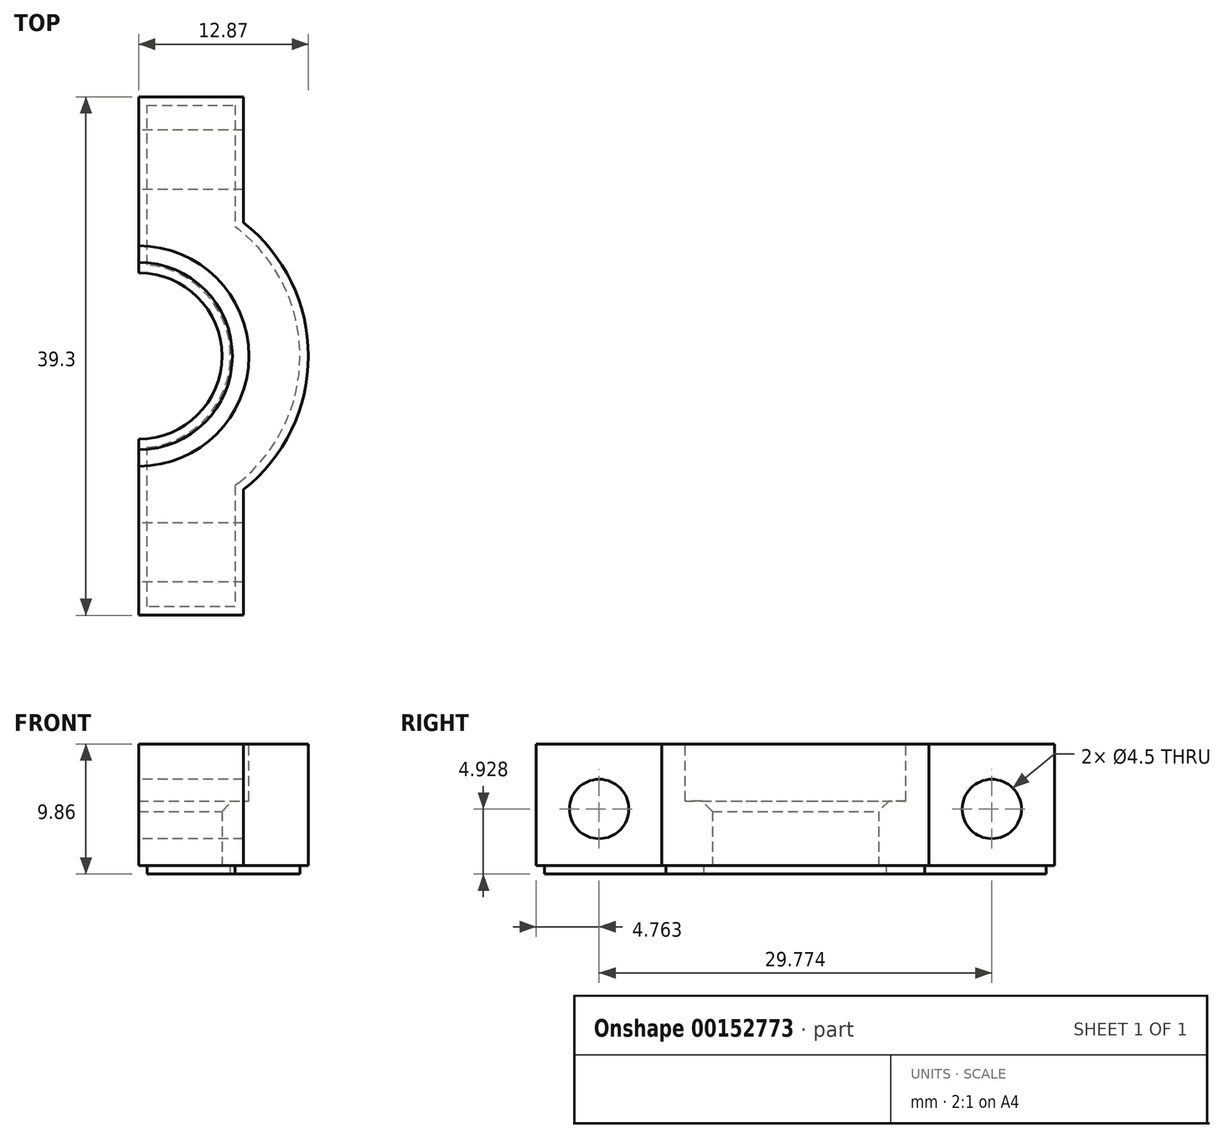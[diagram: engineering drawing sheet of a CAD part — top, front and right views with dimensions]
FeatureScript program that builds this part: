
annotation { "Feature Type Name" : "Feature", "Feature Type Description" : "" }
export const myFeature = defineFeature(function(context is Context, id is Id, definition is map)
    precondition{}
    {
        {
            var Q0;
            Q0=qCreatedBy(makeId("Top.planeOp"),FACE);
            var sketch = newSketch(context, id + "F0", { "sketchPlane" : qUnion([Q0])});
            skArc(sketch, "E0", {"start": v(7.94, -10.12) * mm, "mid": v(12.87, 0) * mm, "end": v(7.94, 10.12) * mm});
            skLineSegment(sketch, "E1", {"start": v(7.94, -10.12) * mm, "end": v(7.94, -19.65) * mm});
            skLineSegment(sketch, "E2", {"start": v(7.94, -19.65) * mm, "end": v(0, -19.65) * mm});
            skLineSegment(sketch, "E3", {"start": v(0, -19.65) * mm, "end": v(0, -6.31) * mm});
            skLineSegment(sketch, "E4", {"start": v(0, -6.31) * mm, "end": v(0, 6.31) * mm, "construction": true});
            skLineSegment(sketch, "E5", {"start": v(0, 6.31) * mm, "end": v(0, 19.65) * mm});
            skLineSegment(sketch, "E6", {"start": v(0, 19.65) * mm, "end": v(7.94, 19.65) * mm});
            skLineSegment(sketch, "E7", {"start": v(7.94, 19.65) * mm, "end": v(7.94, 10.12) * mm});
            skArc(sketch, "E8", {"start": v(0, -6.31) * mm, "mid": v(6.31, 0) * mm, "end": v(0, 6.31) * mm});
            skSolve(sketch);
        }
        {
            var Q0;
            Q0=makeQuery(id+"F0.imprint","IMPRINT",FACE,{"disambiguationData":[TD([[makeQuery(id+"F0.imprint","IMPRINT",EDGE,{"derivedFrom":sQuery(id+"F0.wireOp",EDGE,"1THsXMdy-5DrS-CnlL-Ftxn-9wsGK0M0J4RZ")}),-1.0]])]});
            var Q1;
            Q1=makeQuery(id+"F0.imprint","IMPRINT",FACE,{"disambiguationData":[TD([[makeQuery(id+"F0.imprint","IMPRINT",EDGE,{"derivedFrom":sQuery(id+"F0.wireOp",EDGE,"E0")}),1.0]])]});
            extrude(context, id + "F1", {"entities" : qUnion([Q0, Q1]), "depth" : 9.86 * mm});
        }
        {
            var Q0;
            Q0=makeQuery(id+"F1.opExtrude","SWEPT_FACE",FACE,{"disambiguationData":[OSD([sQuery(id+"F0.wireOp",EDGE,"E2")])]});
            var sketch = newSketch(context, id + "F2", { "sketchPlane" : qUnion([Q0])});
            skLineSegment(sketch, "E9.bottom", {"start": v(0.63, 0) * mm, "end": v(0, 0) * mm});
            skLineSegment(sketch, "E9.top", {"start": v(0.63, 0.63) * mm, "end": v(0, 0.63) * mm});
            skLineSegment(sketch, "E9.left", {"start": v(0.63, 0) * mm, "end": v(0.63, 0.63) * mm});
            skLineSegment(sketch, "E9.right", {"start": v(0, 0) * mm, "end": v(0, 0.63) * mm});
            skSolve(sketch);
        }
        {
            var Q0;
            Q0=makeQuery(id+"F2.imprint","IMPRINT",FACE,{"disambiguationData":[TD([[makeQuery(id+"F2.imprint","IMPRINT",EDGE,{"derivedFrom":sQuery(id+"F2.wireOp",EDGE,"E9.bottom")}),-1.0]])]});
            var Q1;
            Q1=makeQuery(id+"F1.opExtrude","CAP_EDGE",EDGE,{"disambiguationData":[OSD([sQuery(id+"F0.wireOp",EDGE,"E3")])],"isStart":true});
            var Q2;
            Q2=makeQuery(id+"F1.opExtrude","CAP_EDGE",EDGE,{"disambiguationData":[OSD([sQuery(id+"F0.wireOp",EDGE,"E8")])],"isStart":true});
            var Q3;
            Q3=makeQuery(id+"F1.opExtrude","CAP_EDGE",EDGE,{"disambiguationData":[OSD([sQuery(id+"F0.wireOp",EDGE,"E5")])],"isStart":true});
            var Q4;
            Q4=makeQuery(id+"F1.opExtrude","CAP_EDGE",EDGE,{"disambiguationData":[OSD([sQuery(id+"F0.wireOp",EDGE,"E6")])],"isStart":true});
            var Q5;
            Q5=makeQuery(id+"F1.opExtrude","CAP_EDGE",EDGE,{"disambiguationData":[OSD([sQuery(id+"F0.wireOp",EDGE,"E7")])],"isStart":true});
            var Q6;
            Q6=makeQuery(id+"F1.opExtrude","CAP_EDGE",EDGE,{"disambiguationData":[OSD([sQuery(id+"F0.wireOp",EDGE,"E0")])],"isStart":true});
            var Q7;
            Q7=makeQuery(id+"F1.opExtrude","CAP_EDGE",EDGE,{"disambiguationData":[OSD([sQuery(id+"F0.wireOp",EDGE,"E1")])],"isStart":true});
            var Q8;
            Q8=makeQuery(id+"F1.opExtrude","CAP_EDGE",EDGE,{"disambiguationData":[OSD([sQuery(id+"F0.wireOp",EDGE,"E2")])],"isStart":true});
            sweep(context, id + "F3", {"operationType" : NewBodyOperationType.REMOVE, "profiles" : qUnion([Q0]), "path" : qUnion([Q1, Q2, Q3, Q4, Q5, Q6, Q7, Q8])});
        }
        {
            var Q0;
            Q0=makeQuery(id+"F1.opExtrude","CAP_FACE",FACE,{"disambiguationData":[OSD([sQuery(id+"F0.wireOp",EDGE,"E0"),sQuery(id+"F0.wireOp",EDGE,"E1"),sQuery(id+"F0.wireOp",EDGE,"E2"),sQuery(id+"F0.wireOp",EDGE,"E3"),sQuery(id+"F0.wireOp",EDGE,"E5"),sQuery(id+"F0.wireOp",EDGE,"E6"),sQuery(id+"F0.wireOp",EDGE,"E7"),sQuery(id+"F0.wireOp",EDGE,"E8")])],"isStart":false});
            var sketch = newSketch(context, id + "F4", { "sketchPlane" : qUnion([Q0])});
            skLineSegment(sketch, "E10", {"start": v(0, 8.36) * mm, "end": v(0, -8.36) * mm});
            skArc(sketch, "E11", {"start": v(0, -8.36) * mm, "mid": v(8.36, 0) * mm, "end": v(0, 8.36) * mm});
            skSolve(sketch);
        }
        {
            var Q0;
            Q0 = qSketchRegion(id + "F4", true);
            extrude(context, id + "F5", {"entities" : qUnion([Q0]), "operationType" : NewBodyOperationType.REMOVE, "oppositeDirection" : true, "depth" : 4.32 * mm});
        }
        {
            var Q0;
            Q0=makeQuery(id+"F5.boolean.opBoolean","INTERSECT",EDGE,{"derivedFrom":[makeQuery(id+"F1.opExtrude","SWEPT_FACE",FACE,{"disambiguationData":[OSD([sQuery(id+"F0.wireOp",EDGE,"E8")])]}),makeQuery(id+"F5.opExtrude","CAP_FACE",FACE,{"disambiguationData":[OSD([sQuery(id+"F4.wireOp",EDGE,"E10"),sQuery(id+"F4.wireOp",EDGE,"E11")])],"isStart":false})]});
            chamfer(context, id + "F6", {"entities" : qUnion([Q0]), "width" : 0.8 * mm, "tangentPropagation" : true});
        }
        {
            var Q0;
            Q0=makeQuery(id+"F1.opExtrude","SWEPT_FACE",FACE,{"disambiguationData":[OSD([sQuery(id+"F0.wireOp",EDGE,"E5")])]});
            var sketch = newSketch(context, id + "F7", { "sketchPlane" : qUnion([Q0])});
            skLineSegment(sketch, "E12.bottom", {"start": v(-14.89, 9.86) * mm, "end": v(-19.65, 9.86) * mm, "construction": true});
            skLineSegment(sketch, "E12.top", {"start": v(-14.89, 0) * mm, "end": v(-19.65, 0) * mm, "construction": true});
            skLineSegment(sketch, "E12.left", {"start": v(-14.89, 9.86) * mm, "end": v(-14.89, 0) * mm, "construction": true});
            skLineSegment(sketch, "E12.right", {"start": v(-19.65, 9.86) * mm, "end": v(-19.65, 0) * mm, "construction": true});
            skCircle(sketch, "E13", {"center": v(-14.89, 4.93) * mm, "radius": 2.25 * mm});
            skLineSegment(sketch, "E14.bottom", {"start": v(19.65, 9.86) * mm, "end": v(14.89, 9.86) * mm, "construction": true});
            skLineSegment(sketch, "E14.top", {"start": v(19.65, 0) * mm, "end": v(14.89, 0) * mm, "construction": true});
            skLineSegment(sketch, "E14.left", {"start": v(19.65, 9.86) * mm, "end": v(19.65, 0) * mm, "construction": true});
            skLineSegment(sketch, "E14.right", {"start": v(14.89, 9.86) * mm, "end": v(14.89, 0) * mm, "construction": true});
            skCircle(sketch, "E15", {"center": v(14.89, 4.93) * mm, "radius": 2.25 * mm});
            skSolve(sketch);
        }
        {
            var Q0;
            Q0 = qSketchRegion(id + "F7", true);
            var Q1;
            Q1=makeQuery(id+"F1.opExtrude","SWEPT_FACE",FACE,{"disambiguationData":[OSD([sQuery(id+"F0.wireOp",EDGE,"E1")])]});
            extrude(context, id + "F8", {"entities" : qUnion([Q0]), "operationType" : NewBodyOperationType.REMOVE, "endBound" : BoundingType.UP_TO_SURFACE, "oppositeDirection" : true, "endBoundEntityFace" : qUnion([Q1]), "depth" : 25.4 * mm});
        }
    });
